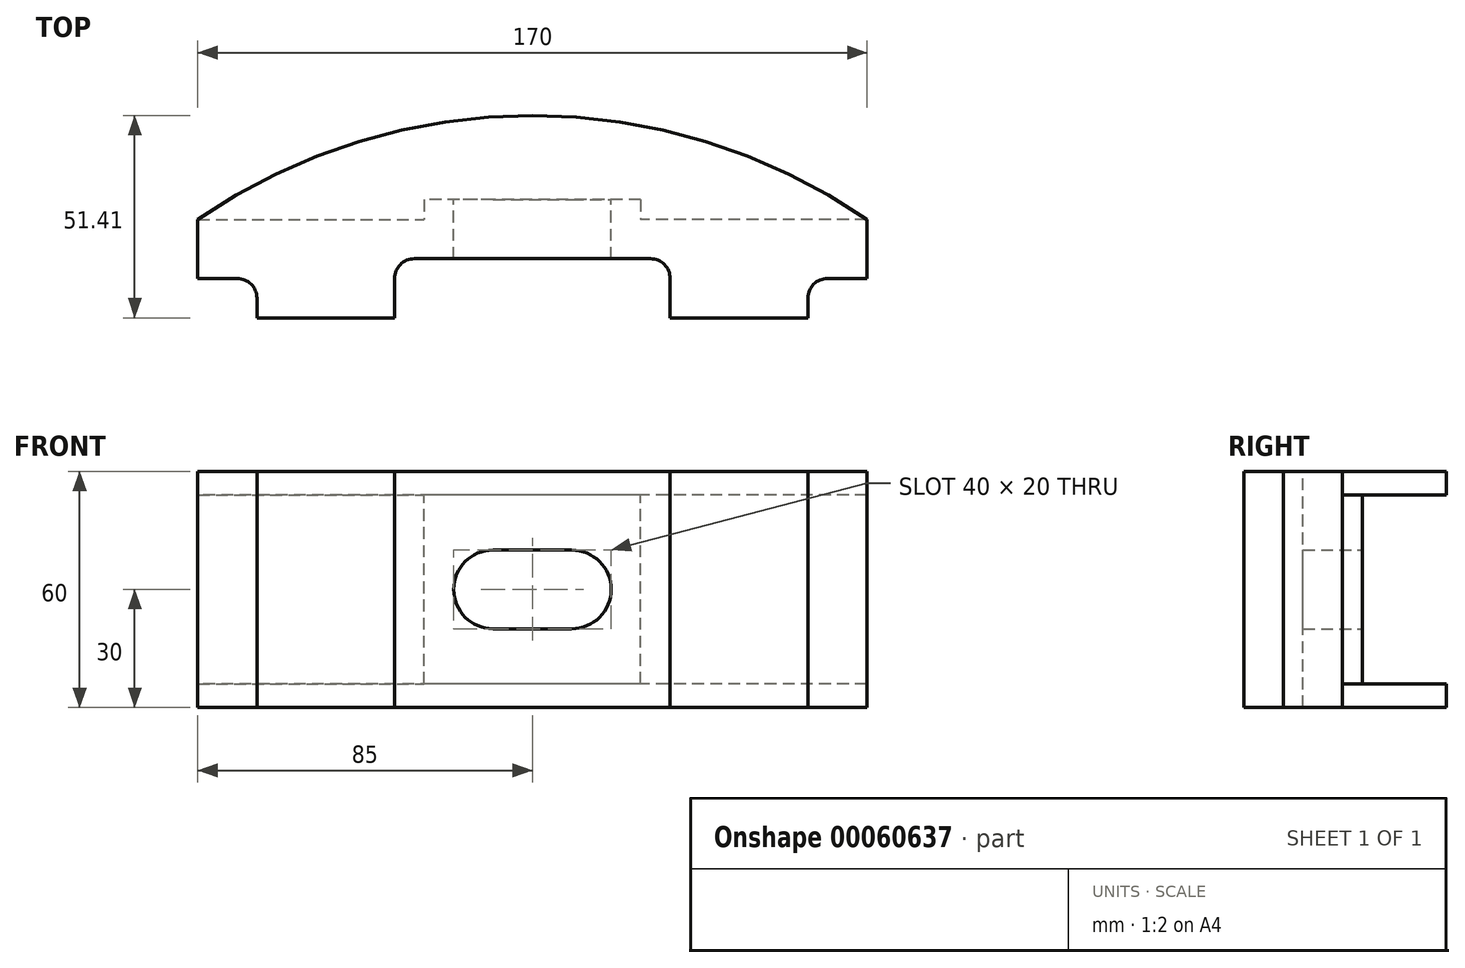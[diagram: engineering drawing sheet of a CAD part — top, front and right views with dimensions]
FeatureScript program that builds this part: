
annotation { "Feature Type Name" : "Feature", "Feature Type Description" : "" }
export const myFeature = defineFeature(function(context is Context, id is Id, definition is map)
    precondition{}
    {
        {
            var Q0;
            Q0=qCreatedBy(makeId("Front.planeOp"),FACE);
            var sketch = newSketch(context, id + "F0", { "sketchPlane" : qUnion([Q0])});
            skLineSegment(sketch, "E0.rect.bottom", {"start": v(85, 30) * mm, "end": v(-85, 30) * mm});
            skLineSegment(sketch, "E0.rect.top", {"start": v(85, -30) * mm, "end": v(-85, -30) * mm});
            skLineSegment(sketch, "E0.rect.left", {"start": v(85, 30) * mm, "end": v(85, -30) * mm});
            skLineSegment(sketch, "E0.rect.right", {"start": v(-85, 30) * mm, "end": v(-85, -30) * mm});
            skPoint(sketch, "E0.rect.middle", {"position": v(0, 0) * mm});
            skSolve(sketch);
        }
        {
            var Q0;
            Q0 = qSketchRegion(id + "F0", true);
            extrude(context, id + "F1", {"entities" : qUnion([Q0]), "depth" : 30 * mm});
        }
        {
            var Q0;
            Q0=qCreatedBy(makeId("Top.planeOp"),FACE);
            var sketch = newSketch(context, id + "F2", { "sketchPlane" : qUnion([Q0])});
            skLineSegment(sketch, "E1.rect.bottom", {"start": v(35, -15) * mm, "end": v(-35, -15) * mm});
            skLineSegment(sketch, "E1.rect.top", {"start": v(35, -45) * mm, "end": v(-35, -45) * mm});
            skLineSegment(sketch, "E1.rect.left", {"start": v(35, -15) * mm, "end": v(35, -45) * mm});
            skLineSegment(sketch, "E1.rect.right", {"start": v(-35, -15) * mm, "end": v(-35, -45) * mm});
            skPoint(sketch, "E1.rect.middle", {"position": v(0, -30) * mm});
            skPoint(sketch, "E2.rect.middle", {"position": v(17.94, 30.97) * mm});
            skSolve(sketch);
        }
        {
            var Q0;
            Q0=makeQuery(id+"F2.imprint","IMPRINT",FACE,{"disambiguationData":[TD([[makeQuery(id+"F2.imprint","IMPRINT",EDGE,{"derivedFrom":sQuery(id+"F2.wireOp",EDGE,"E1.rect.bottom")}),1.0]])]});
            extrude(context, id + "F3", {"entities" : qUnion([Q0]), "operationType" : NewBodyOperationType.REMOVE, "endBound" : BoundingType.SYMMETRIC, "oppositeDirection" : true, "depth" : 119.38 * mm});
        }
        {
            var Q0;
            Q0=makeQuery(id+"F3.boolean.opBoolean","COPY",EDGE,{"derivedFrom":makeQuery(id+"F3.opExtrude","SWEPT_EDGE",EDGE,{"disambiguationData":[OSD([sQuery(id+"F2.wireOp",EDGE,"E1.rect.bottom"),sQuery(id+"F2.wireOp",EDGE,"E1.rect.left")])]})});
            var Q1;
            Q1=makeQuery(id+"F3.boolean.opBoolean","COPY",EDGE,{"derivedFrom":makeQuery(id+"F3.opExtrude","SWEPT_EDGE",EDGE,{"disambiguationData":[OSD([sQuery(id+"F2.wireOp",EDGE,"E1.rect.bottom"),sQuery(id+"F2.wireOp",EDGE,"E1.rect.right")])]})});
            fillet(context, id + "F4", {"entities" : qUnion([Q0, Q1]), "radius" : 5 * mm, "tangentPropagation" : true, "allowEdgeOverflow" : false});
        }
        {
            var Q0;
            Q0=makeQuery(id+"F1.opExtrude","SWEPT_FACE",FACE,{"disambiguationData":[OSD([sQuery(id+"F0.wireOp",EDGE,"E0.rect.bottom")])]});
            var sketch = newSketch(context, id + "F5", { "sketchPlane" : qUnion([Q0])});
            skLineSegment(sketch, "E3.bottom", {"start": v(85, -30) * mm, "end": v(70, -30) * mm});
            skLineSegment(sketch, "E3.top", {"start": v(85, -20) * mm, "end": v(75, -20) * mm});
            skLineSegment(sketch, "E3.left", {"start": v(85, -30) * mm, "end": v(85, -20) * mm});
            skLineSegment(sketch, "E3.right", {"start": v(70, -30) * mm, "end": v(70, -25) * mm});
            skLineSegment(sketch, "E4.bottom", {"start": v(-85, -30) * mm, "end": v(-70, -30) * mm});
            skLineSegment(sketch, "E4.top", {"start": v(-85, -20) * mm, "end": v(-75, -20) * mm});
            skLineSegment(sketch, "E4.left", {"start": v(-85, -30) * mm, "end": v(-85, -20) * mm});
            skLineSegment(sketch, "E4.right", {"start": v(-70, -30) * mm, "end": v(-70, -25) * mm});
            skPoint(sketch, "E5.visualSharp", {"position": v(70, -20) * mm});
            skArc(sketch, "E5.filletArc", {"start": v(75, -20) * mm, "mid": v(71.46, -21.46) * mm, "end": v(70, -25) * mm});
            skPoint(sketch, "E6.visualSharp", {"position": v(-70, -20) * mm});
            skArc(sketch, "E6.filletArc", {"start": v(-70, -25) * mm, "mid": v(-71.46, -21.46) * mm, "end": v(-75, -20) * mm});
            skSolve(sketch);
        }
        {
            var Q0;
            Q0 = qSketchRegion(id + "F5", true);
            extrude(context, id + "F6", {"entities" : qUnion([Q0]), "operationType" : NewBodyOperationType.REMOVE, "endBound" : BoundingType.THROUGH_ALL, "oppositeDirection" : true, "depth" : 25 * mm});
        }
        {
            var Q0;
            Q0=makeQuery(id+"F1.opExtrude","SWEPT_FACE",FACE,{"disambiguationData":[OSD([sQuery(id+"F0.wireOp",EDGE,"E0.rect.bottom")])]});
            var sketch = newSketch(context, id + "F7", { "sketchPlane" : qUnion([Q0])});
            skLineSegment(sketch, "E7.bottom", {"start": v(85, 0) * mm, "end": v(27.5, 0) * mm});
            skLineSegment(sketch, "E7.top", {"start": v(85, -5) * mm, "end": v(27.5, -5) * mm});
            skLineSegment(sketch, "E7.left", {"start": v(85, 0) * mm, "end": v(85, -5) * mm});
            skLineSegment(sketch, "E7.right", {"start": v(27.5, 0) * mm, "end": v(27.5, -5) * mm});
            skLineSegment(sketch, "E8.bottom", {"start": v(-85, 0) * mm, "end": v(-27.5, 0) * mm});
            skLineSegment(sketch, "E8.top", {"start": v(-85, -5) * mm, "end": v(-27.5, -5) * mm});
            skLineSegment(sketch, "E8.left", {"start": v(-85, 0) * mm, "end": v(-85, -5) * mm});
            skLineSegment(sketch, "E8.right", {"start": v(-27.5, 0) * mm, "end": v(-27.5, -5) * mm});
            skSolve(sketch);
        }
        {
            var Q0;
            Q0 = qSketchRegion(id + "F7", true);
            extrude(context, id + "F8", {"entities" : qUnion([Q0]), "operationType" : NewBodyOperationType.REMOVE, "endBound" : BoundingType.THROUGH_ALL, "oppositeDirection" : true, "depth" : 25 * mm});
        }
        {
            var Q0;
            Q0=makeQuery(id+"F1.opExtrude","SWEPT_FACE",FACE,{"disambiguationData":[OSD([sQuery(id+"F0.wireOp",EDGE,"E0.rect.bottom")])]});
            var sketch = newSketch(context, id + "F9", { "sketchPlane" : qUnion([Q0])});
            skArc(sketch, "E9", {"start": v(85, -5) * mm, "mid": v(0, 21.4) * mm, "end": v(-85, -5) * mm});
            skSolve(sketch);
        }
        {
            var Q0;
            Q0=makeQuery(id+"F9.imprint","IMPRINT",FACE,{"disambiguationData":[TD([[makeQuery(id+"F9.imprint","IMPRINT",EDGE,{"derivedFrom":sQuery(id+"F9.wireOp",EDGE,"E9")}),1.0]])]});
            extrude(context, id + "F10", {"entities" : qUnion([Q0]), "operationType" : NewBodyOperationType.ADD, "oppositeDirection" : true, "depth" : 6 * mm});
        }
        {
            var Q0;
            Q0=makeQuery(id+"F1.opExtrude","SWEPT_BODY",BODY,{"disambiguationData":[OSD([sQuery(id+"F0.wireOp",EDGE,"E0.rect.bottom"),sQuery(id+"F0.wireOp",EDGE,"E0.rect.top"),sQuery(id+"F0.wireOp",EDGE,"E0.rect.left"),sQuery(id+"F0.wireOp",EDGE,"E0.rect.right")])]});
            var Q1;
            {var subQ0=sQuery(id+"F0.wireOp",EDGE,"E0.rect.bottom");Q1=makeQuery(id+"F10.boolean.opBoolean","MERGE",FACE,{"derivedFrom":[makeQuery(id+"F1.opExtrude","SWEPT_FACE",FACE,{"disambiguationData":[OSD([subQ0])]}),makeQuery(id+"F10.opExtrude","CAP_FACE",FACE,{"disambiguationData":[OSD([subQ0,sQuery(id+"F7.wireOp",EDGE,"E7.top"),sQuery(id+"F7.wireOp",EDGE,"E7.right"),sQuery(id+"F7.wireOp",EDGE,"E8.top"),sQuery(id+"F7.wireOp",EDGE,"E8.right"),sQuery(id+"F9.wireOp",EDGE,"E9")])],"isStart":true})]});}
            var Q2;
            Q2=qCreatedBy(makeId("Top.planeOp"),FACE);
            mirror(context, id + "F11", {"operationType" : NewBodyOperationType.ADD, "entities" : qUnion([Q0]), "faces" : qUnion([Q1]), "mirrorPlane" : qUnion([Q2])});
        }
        {
            var Q0;
            Q0=makeQuery(id+"F1.opExtrude","CAP_FACE",FACE,{"disambiguationData":[OSD([sQuery(id+"F0.wireOp",EDGE,"E0.rect.bottom"),sQuery(id+"F0.wireOp",EDGE,"E0.rect.top"),sQuery(id+"F0.wireOp",EDGE,"E0.rect.left"),sQuery(id+"F0.wireOp",EDGE,"E0.rect.right")])],"isStart":true});
            var sketch = newSketch(context, id + "F12", { "sketchPlane" : qUnion([Q0])});
            skLineSegment(sketch, "E10.rect.bottom", {"start": v(10, 10) * mm, "end": v(-10, 10) * mm});
            skLineSegment(sketch, "E10.rect.top", {"start": v(10, -10) * mm, "end": v(-10, -10) * mm});
            skLineSegment(sketch, "E10.rect.left", {"start": v(20, 0) * mm, "end": v(20, 0) * mm});
            skLineSegment(sketch, "E10.rect.right", {"start": v(-20, 0) * mm, "end": v(-20, 0) * mm});
            skPoint(sketch, "E10.rect.middle", {"position": v(0, 0) * mm});
            skPoint(sketch, "E11.visualSharp", {"position": v(20, 10) * mm});
            skArc(sketch, "E11.filletArc", {"start": v(20, 0) * mm, "mid": v(17.07, 7.07) * mm, "end": v(10, 10) * mm});
            skPoint(sketch, "E12.visualSharp", {"position": v(-20, 10) * mm});
            skArc(sketch, "E12.filletArc", {"start": v(-10, 10) * mm, "mid": v(-17.07, 7.07) * mm, "end": v(-20, 0) * mm});
            skPoint(sketch, "E13.visualSharp", {"position": v(-20, -10) * mm});
            skArc(sketch, "E13.filletArc", {"start": v(-20, 0) * mm, "mid": v(-17.07, -7.07) * mm, "end": v(-10, -10) * mm});
            skPoint(sketch, "E14.visualSharp", {"position": v(20, -10) * mm});
            skArc(sketch, "E14.filletArc", {"start": v(10, -10) * mm, "mid": v(17.07, -7.07) * mm, "end": v(20, 0) * mm});
            skSolve(sketch);
        }
        {
            var Q0;
            Q0 = qSketchRegion(id + "F12", true);
            extrude(context, id + "F13", {"entities" : qUnion([Q0]), "operationType" : NewBodyOperationType.REMOVE, "endBound" : BoundingType.THROUGH_ALL, "oppositeDirection" : true, "depth" : 25 * mm});
        }
    });
